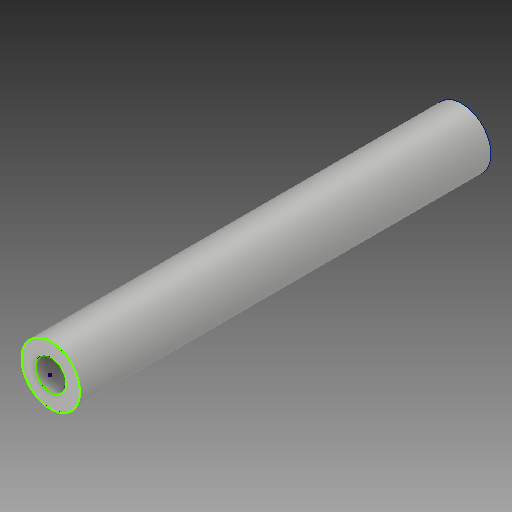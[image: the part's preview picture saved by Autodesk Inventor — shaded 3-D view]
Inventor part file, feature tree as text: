
AUTODESK INVENTOR PART (.ipt)
format: ipt  version: 2017 (Build 210142000, 142)  size: 95,744 bytes
history: native  units: in
note: dims shown in document units (in); Inventor stores cm internally (conversion verified against a paired STEP export)
features: sketch x2, extrude x1
ambient origin geometry x8: Origin, YZ Plane, XZ Plane, XY Plane, X Axis, Y Axis, Z Axis, Center Point
bodies: Solid1 (feature_tree)
feature tree (3):
  extrude  "Extrusion1"  [1 undecoded]
  sketch  "Sketch3"
  sketch  "Sketch1"  dims[d0=3.5in d1=0.0in]
note: 1 required parameter value undecoded (feature->parameter linkage not recoverable at this tier; creation-order binding heuristic only, values carry confidence <= 0.55)
